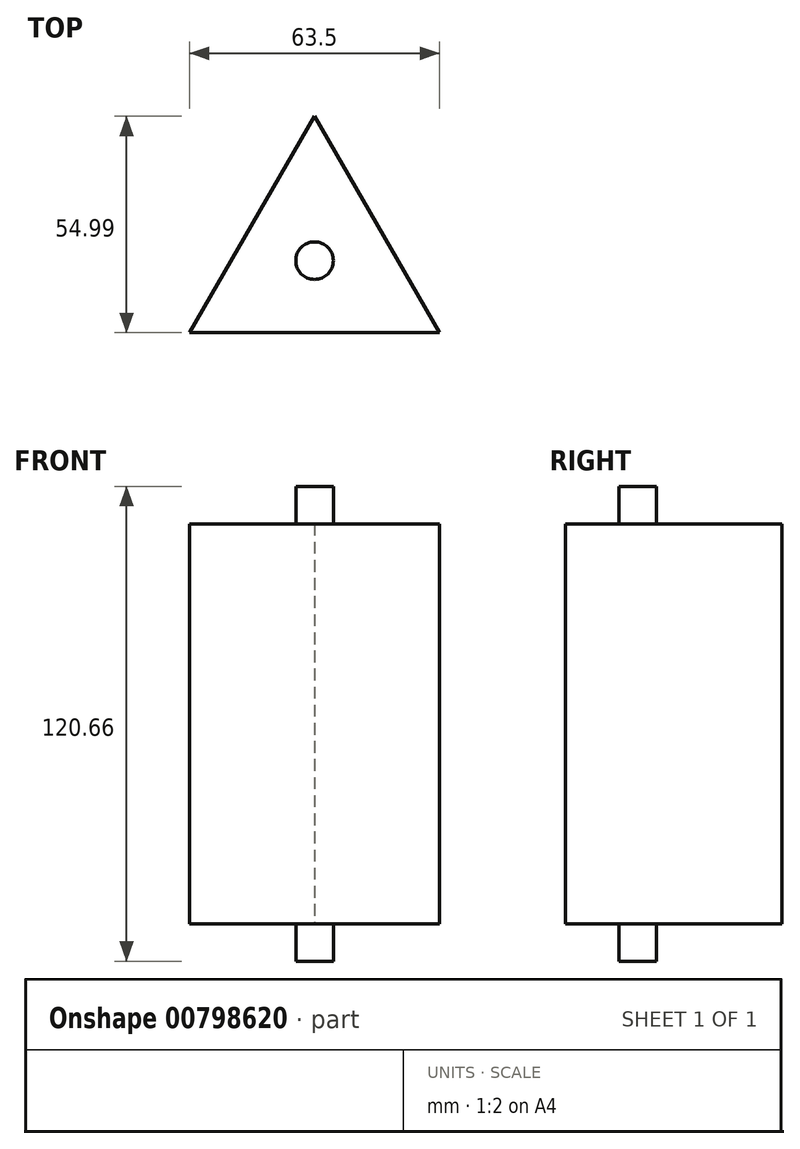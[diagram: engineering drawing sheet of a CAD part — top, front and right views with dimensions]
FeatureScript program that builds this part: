
annotation { "Feature Type Name" : "Feature", "Feature Type Description" : "" }
export const myFeature = defineFeature(function(context is Context, id is Id, definition is map)
    precondition{}
    {
        {
            var Q0;
            Q0=qCreatedBy(makeId("Top.planeOp"),FACE);
            var sketch = newSketch(context, id + "F0", { "sketchPlane" : qUnion([Q0])});
            skCircle(sketch, "E0.cCircle", {"center": v(0, 0) * mm, "radius": 36.66 * mm, "construction": true});
            skLineSegment(sketch, "E0.0", {"start": v(0, 36.66) * mm, "end": v(31.75, -18.33) * mm});
            skLineSegment(sketch, "E0.1", {"start": v(31.75, -18.33) * mm, "end": v(-31.75, -18.33) * mm});
            skLineSegment(sketch, "E0.2", {"start": v(-31.75, -18.33) * mm, "end": v(0, 36.66) * mm});
            skSolve(sketch);
        }
        {
            var Q0;
            Q0 = qSketchRegion(id + "F0", true);
            extrude(context, id + "F1", {"entities" : qUnion([Q0]), "endBound" : BoundingType.SYMMETRIC, "depth" : 101.6 * mm, "offsetDistance" : 25.4 * mm});
        }
        {
            var Q0;
            Q0=qCreatedBy(makeId("Top.planeOp"),FACE);
            var sketch = newSketch(context, id + "F2", { "sketchPlane" : qUnion([Q0])});
            skCircle(sketch, "E1", {"center": v(0, 0) * mm, "radius": 4.76 * mm});
            skSolve(sketch);
        }
        {
            var Q0;
            Q0 = qSketchRegion(id + "F2", true);
            extrude(context, id + "F3", {"entities" : qUnion([Q0]), "operationType" : NewBodyOperationType.ADD, "endBound" : BoundingType.SYMMETRIC, "depth" : 120.65 * mm, "offsetDistance" : 25.4 * mm});
        }
    });
